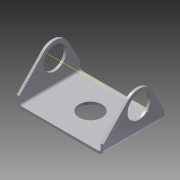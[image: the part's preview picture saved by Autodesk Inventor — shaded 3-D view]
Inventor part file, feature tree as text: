
AUTODESK INVENTOR PART (.ipt)
format: ipt  version: 2013 (Build 170138000, 138)  size: 200,192 bytes
history: native  units: in
note: dims shown in document units (in); Inventor stores cm internally (conversion verified against a paired STEP export)
features: other x8, sheet_metal_op x7, sketch x5
ambient origin geometry x8: Origin, YZ Plane, XZ Plane, XY Plane, X Axis, Y Axis, Z Axis, Center Point
bodies: Solid1 (feature_tree)
feature tree (20):
  sheet_metal_op  "Face1"
  sheet_metal_op  "Flange1"
  sheet_metal_op  "Flange2"
  other  "Work Axis1"
  sketch  "Sketch1"  dims[d0=4.0in]
  other  "Plate1"
  sketch  "Sketch2"  dims[d2=3.0in]
  other  "Plate2"
  sheet_metal_op  "Bend1"
  sheet_metal_op  "Corner1"
  sketch  "Sketch3"  dims[d3=0.125in]
  other  "Plate3"
  sheet_metal_op  "Bend2"
  sheet_metal_op  "Corner2"
  sketch  "Sketch4"  dims[d4=0.125in]
  sketch  "Sketch6"  dims[d5=0.0625in d6=0.25in d7=0.125in d8=2.0in d9=90.0deg d10=0.125in d11=0.5in d12=0.125in d13=0.125in d14=0.125in d15=0.0625in d16=0.25in d17=0.125in d18=2.0in d19=90.0deg d20=0.125in d21=0.5in d22=0.125in d23=0.125in d24=1.125in d25=0.75in d26=200.0in d27=0.0in d28=0.25in d29=0.25in d30=20.0in d31=0.0in d32=1.125in d33=0.125in d34=0.0in d35=1.5in d36=1.875in]
  other  "Cut1"
  other  "Cut2"
  other  "Cut3"
  other  "Definition1"
